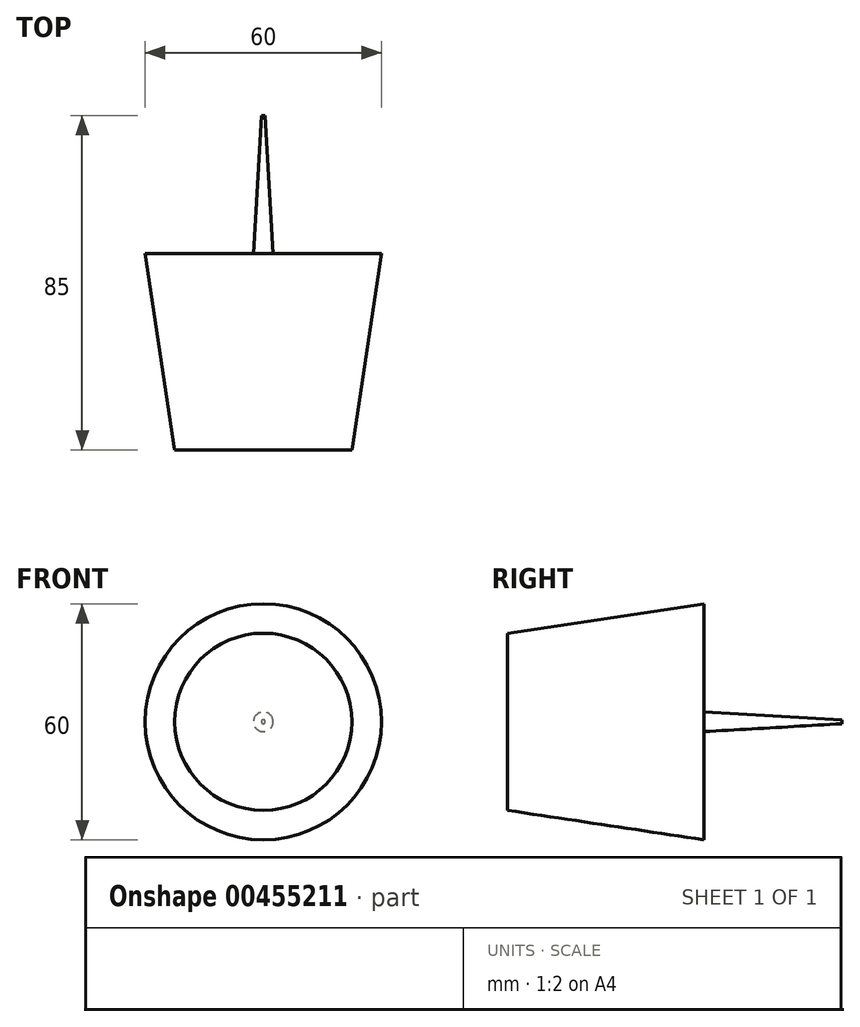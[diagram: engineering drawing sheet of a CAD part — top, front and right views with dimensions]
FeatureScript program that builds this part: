
annotation { "Feature Type Name" : "Feature", "Feature Type Description" : "" }
export const myFeature = defineFeature(function(context is Context, id is Id, definition is map)
    precondition{}
    {
        {
            var Q0;
            Q0=qCreatedBy(makeId("Front.planeOp"),FACE);
            var sketch = newSketch(context, id + "F0", { "sketchPlane" : qUnion([Q0])});
            skCircle(sketch, "E0", {"center": v(0, 0) * mm, "radius": 30 * mm});
            skSolve(sketch);
        }
        {
            var Q0;
            Q0=makeQuery(id+"F0.imprint","IMPRINT",FACE,{"disambiguationData":[TD([[makeQuery(id+"F0.imprint","IMPRINT",EDGE,{"derivedFrom":sQuery(id+"F0.wireOp",EDGE,"E0")}),1.0]])]});
            cPlane(context, id + "F1", {"entities" : qUnion([Q0]), "cplaneType" : CPlaneType.OFFSET, "offset" : 50 * mm, "width" : 150 * mm, "height" : 150 * mm});
        }
        {
            var Q0;
            Q0=qCreatedBy(id+"F1.planeOp",FACE);
            var sketch = newSketch(context, id + "F2", { "sketchPlane" : qUnion([Q0])});
            skCircle(sketch, "E1", {"center": v(0, 0) * mm, "radius": 22.5 * mm});
            skSolve(sketch);
        }
        {
            var Q0;
            Q0=makeQuery(id+"F0.imprint","IMPRINT",FACE,{"disambiguationData":[TD([[makeQuery(id+"F0.imprint","IMPRINT",EDGE,{"derivedFrom":sQuery(id+"F0.wireOp",EDGE,"E0")}),1.0]])]});
            var Q1;
            Q1=makeQuery(id+"F2.imprint","IMPRINT",FACE,{"disambiguationData":[TD([[makeQuery(id+"F2.imprint","IMPRINT",EDGE,{"derivedFrom":sQuery(id+"F2.wireOp",EDGE,"E1")}),1.0]])]});
            loft(context, id + "F3", {"sheetProfilesArray" : [{ "sheetProfileEntities" : qUnion([Q0]) }, { "sheetProfileEntities" : qUnion([Q1]) }]});
        }
        {
            var Q0;
            Q0=qCreatedBy(makeId("Front.planeOp"),FACE);
            var sketch = newSketch(context, id + "F4", { "sketchPlane" : qUnion([Q0])});
            skCircle(sketch, "E2", {"center": v(0, 0) * mm, "radius": 2.5 * mm});
            skSolve(sketch);
        }
        {
            var Q0;
            Q0=qCreatedBy(makeId("Front.planeOp"),FACE);
            cPlane(context, id + "F5", {"entities" : qUnion([Q0]), "cplaneType" : CPlaneType.OFFSET, "offset" : 35 * mm, "oppositeDirection" : true, "width" : 150 * mm, "height" : 150 * mm});
        }
        {
            var Q0;
            Q0=qCreatedBy(id+"F5.planeOp",FACE);
            var sketch = newSketch(context, id + "F6", { "sketchPlane" : qUnion([Q0])});
            skCircle(sketch, "E3", {"center": v(0, 0) * mm, "radius": 0.5 * mm});
            skSolve(sketch);
        }
        {
            var Q1;
            Q1=makeQuery(id+"F4.imprint","IMPRINT",FACE,{"disambiguationData":[TD([[makeQuery(id+"F4.imprint","IMPRINT",EDGE,{"derivedFrom":sQuery(id+"F4.wireOp",EDGE,"E2")}),1.0]])]});
            var Q2;
            Q2=makeQuery(id+"F6.imprint","IMPRINT",FACE,{"disambiguationData":[TD([[makeQuery(id+"F6.imprint","IMPRINT",EDGE,{"derivedFrom":sQuery(id+"F6.wireOp",EDGE,"E3")}),1.0]])]});
            loft(context, id + "F7", {"operationType" : NewBodyOperationType.ADD, "sheetProfilesArray" : [{ "sheetProfileEntities" : qUnion([Q1]) }, { "sheetProfileEntities" : qUnion([Q2]) }]});
        }
    });
